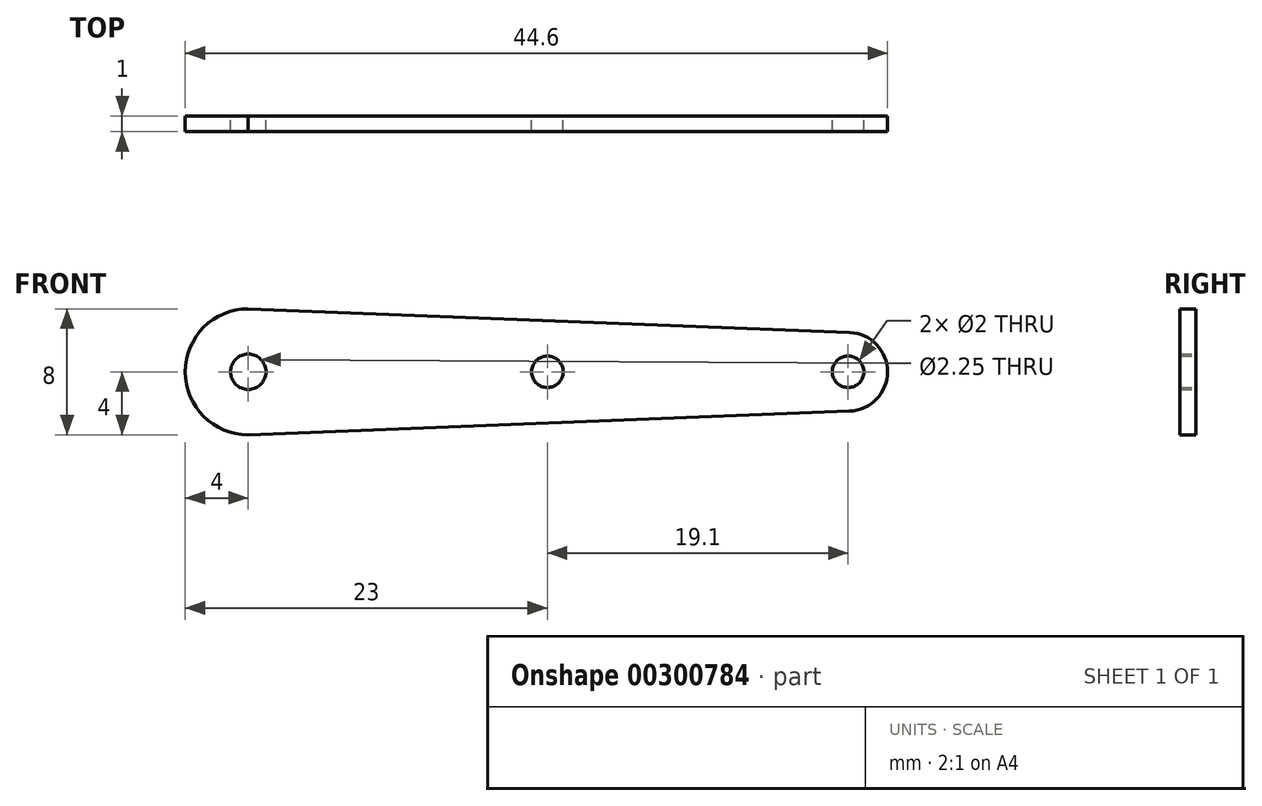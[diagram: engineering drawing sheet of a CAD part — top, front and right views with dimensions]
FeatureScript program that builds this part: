
annotation { "Feature Type Name" : "Feature", "Feature Type Description" : "" }
export const myFeature = defineFeature(function(context is Context, id is Id, definition is map)
    precondition{}
    {
        {
            var Q0;
            Q0=qCreatedBy(makeId("Front.planeOp"),FACE);
            var sketch = newSketch(context, id + "F0", { "sketchPlane" : qUnion([Q0])});
            skCircle(sketch, "E0", {"center": v(0, 0) * mm, "radius": 1.13 * mm});
            skCircle(sketch, "E1", {"center": v(38.1, 0) * mm, "radius": 1 * mm});
            skArc(sketch, "E2", {"start": v(0, 4) * mm, "mid": v(-4, 0) * mm, "end": v(0, -4) * mm});
            skArc(sketch, "E3", {"start": v(38.2, -2.5) * mm, "mid": v(40.6, 0) * mm, "end": v(38.2, 2.5) * mm});
            skLineSegment(sketch, "E4", {"start": v(0, -4) * mm, "end": v(38.2, -2.5) * mm});
            skLineSegment(sketch, "E5", {"start": v(0, 4) * mm, "end": v(38.2, 2.5) * mm});
            skCircle(sketch, "E6", {"center": v(19, 0) * mm, "radius": 1 * mm});
            skSolve(sketch);
        }
        {
            var Q0;
            Q0 = qSketchRegion(id + "F0", true);
            extrude(context, id + "F1", {"entities" : qUnion([Q0]), "depth" : 1 * mm});
        }
    });
